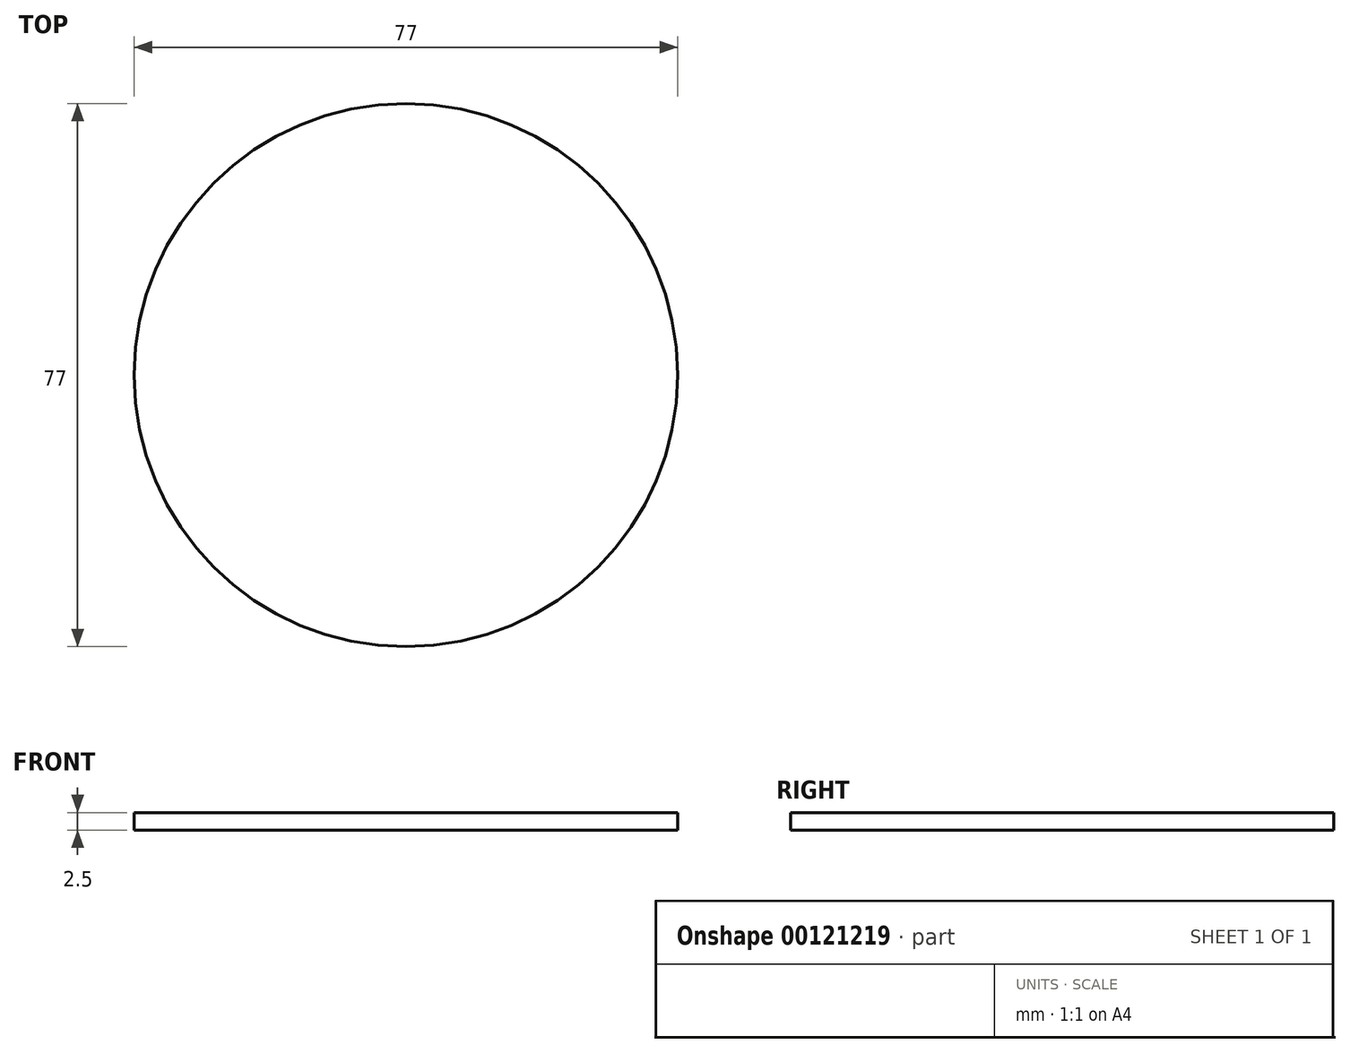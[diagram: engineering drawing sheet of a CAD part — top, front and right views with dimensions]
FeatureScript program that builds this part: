
annotation { "Feature Type Name" : "Feature", "Feature Type Description" : "" }
export const myFeature = defineFeature(function(context is Context, id is Id, definition is map)
    precondition{}
    {
        {
            var Q0;
            Q0=qCreatedBy(makeId("Top.planeOp"),FACE);
            var sketch = newSketch(context, id + "F0", { "sketchPlane" : qUnion([Q0])});
            skCircle(sketch, "E0", {"center": v(0, 0) * mm, "radius": 38.5 * mm});
            skSolve(sketch);
        }
        {
            var Q0;
            Q0 = qSketchRegion(id + "F0", true);
            extrude(context, id + "F1", {"entities" : qUnion([Q0]), "depth" : 2.5 * mm});
        }
    });
